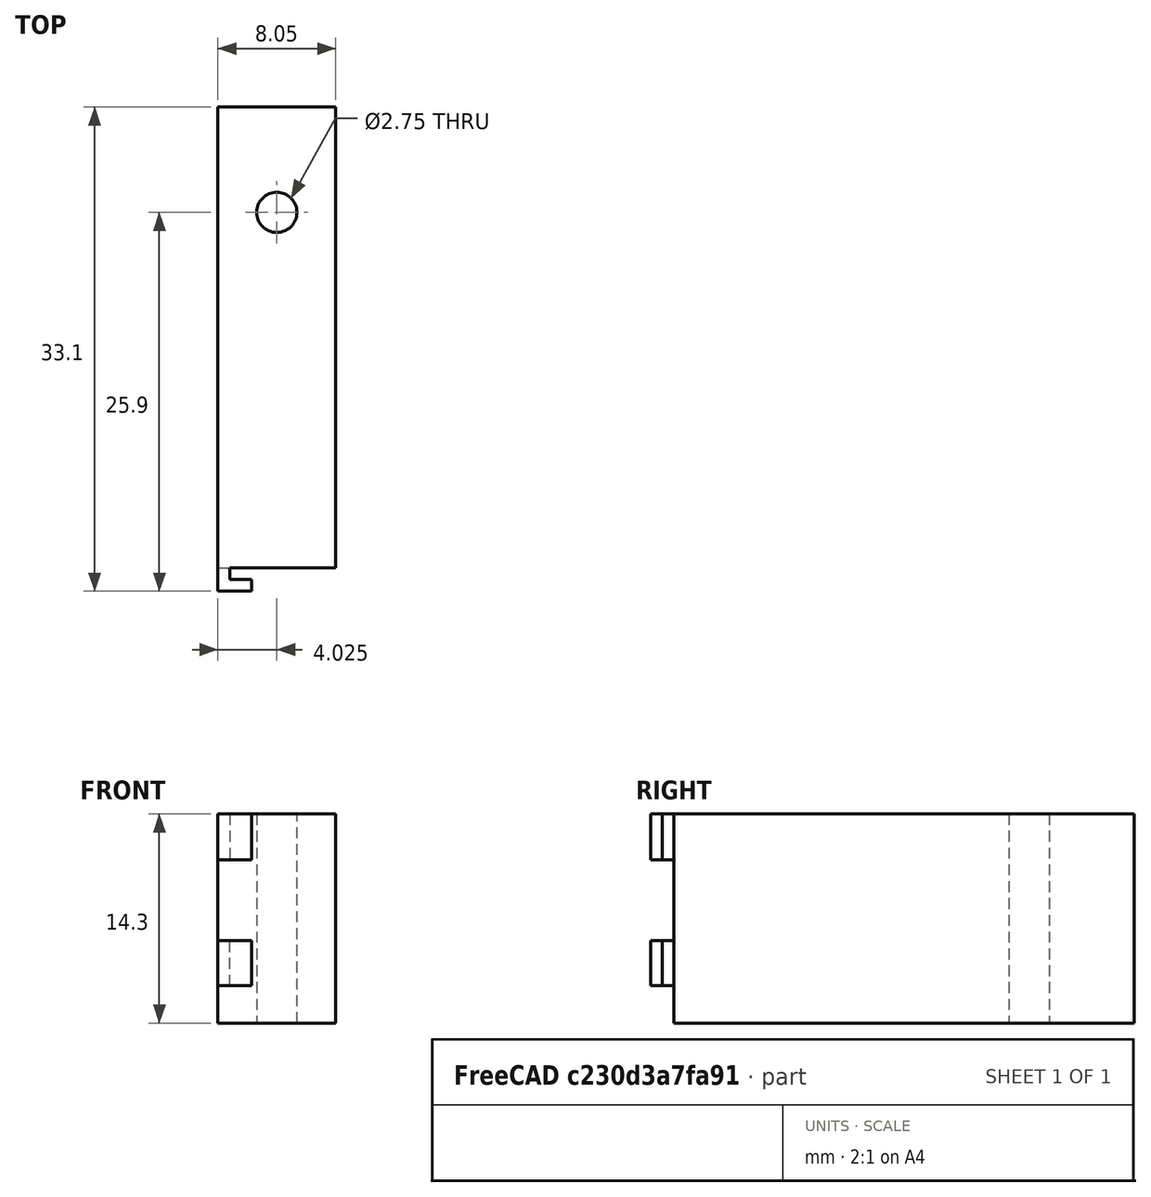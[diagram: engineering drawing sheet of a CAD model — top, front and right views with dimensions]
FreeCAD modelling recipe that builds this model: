
FCSTD DOCUMENT  (FreeCAD 0.19R)
Label: Retention Bracket
License: All rights reserved
LicenseURL: http://en.wikipedia.org/wiki/All_rights_reserved
objects: Sketcher::SketchObject×3, PartDesign::Pad×3, PartDesign::Body×1, Mesh::Feature×1
note: 10 computed .brp shape members not serialized (recipe doc carries the construction recipe); baked Part::Feature solids carry a one-line shape summary decoded from their .brp

FEATURE [Sketcher::SketchObject] Sketch
  FullyConstrained = true
  MapMode = 5
  Support = -> [XY_Plane]
  sketch-geometry (7):
    g0: LineSegment StartX=0 StartY=0 StartZ=0 EndX=8.05 EndY=0 EndZ=0
    g1: LineSegment StartX=8.05 StartY=0 StartZ=0 EndX=8.05 EndY=31.5 EndZ=0
    g2: LineSegment StartX=8.05 StartY=31.5 StartZ=0 EndX=0 EndY=31.5 EndZ=0
    g3: LineSegment StartX=0 StartY=31.5 StartZ=0 EndX=0 EndY=0 EndZ=0
    g4: Circle CenterX=4.025 CenterY=24.3 CenterZ=0 NormalX=0 NormalY=0 NormalZ=1 AngleXU=0 Radius=1.375
    g5: LineSegment StartX=4.025 StartY=24.3 StartZ=0 EndX=0 EndY=24.3 EndZ=0
    g6: LineSegment StartX=4.025 StartY=24.3 StartZ=0 EndX=8.05 EndY=24.3 EndZ=0
  constraints (20):
    c: Coincident(g0,g1)
    c: Coincident(g1,g2)
    c: Coincident(g2,g3)
    c: Coincident(g3,g0)
    c: Horizontal(g0)
    c: Horizontal(g2)
    c: Vertical(g1)
    c: Vertical(g3)
    c: Coincident(g0,g-1)
    c: DistanceY(g1,g1) = 31.5
    c: DistanceX(g2,g2) = 8.05
    c: Radius(g4) = 1.375
    c: Coincident(g5,g4)
    c: PointOnObject(g5,g3)
    c: Horizontal(g5)
    c: Coincident(g6,g4)
    c: PointOnObject(g6,g1)
    c: Horizontal(g6)
    c: Equal(g5,g6)
    c: DistanceY(g0,g4) = 24.3
FEATURE [PartDesign::Pad] Pad
  Direction = (1,1,1)
  Length = 14.3
  Length2 = 100
  Profile = -> Sketch
  Type = 0
FEATURE [Sketcher::SketchObject] Sketch001
  ExternalGeometry = -> [Pad]
  FullyConstrained = true
  MapMode = 5
  Placement = pos=(0,0,0) rot=(1,0,0;1.5708rad)
  Support = -> [Pad]
  sketch-geometry (8):
    g0: LineSegment StartX=0 StartY=14.3 StartZ=0 EndX=0.8 EndY=14.3 EndZ=0
    g1: LineSegment StartX=0.8 StartY=14.3 StartZ=0 EndX=0.8 EndY=11.15 EndZ=0
    g2: LineSegment StartX=0.8 StartY=11.15 StartZ=0 EndX=0 EndY=11.15 EndZ=0
    g3: LineSegment StartX=0 StartY=11.15 StartZ=0 EndX=0 EndY=14.3 EndZ=0
    g4: LineSegment StartX=0 StartY=2.55 StartZ=0 EndX=0.8 EndY=2.55 EndZ=0
    g5: LineSegment StartX=0.8 StartY=2.55 StartZ=0 EndX=0.8 EndY=5.65 EndZ=0
    g6: LineSegment StartX=0.8 StartY=5.65 StartZ=0 EndX=0 EndY=5.65 EndZ=0
    g7: LineSegment StartX=0 StartY=5.65 StartZ=0 EndX=0 EndY=2.55 EndZ=0
  constraints (23):
    c: Coincident(g0,g1)
    c: Coincident(g1,g2)
    c: Coincident(g2,g3)
    c: Coincident(g3,g0)
    c: Horizontal(g0)
    c: Horizontal(g2)
    c: Vertical(g1)
    c: Vertical(g3)
    c: Coincident(g4,g5)
    c: Coincident(g5,g6)
    c: Coincident(g6,g7)
    c: Coincident(g7,g4)
    c: Horizontal(g4)
    c: Horizontal(g6)
    c: Vertical(g5)
    c: Vertical(g7)
    c: PointOnObject(g4,g-3)
    c: DistanceY(g1,g1) = 3.15
    c: DistanceY(g5,g5) = 3.1
    c: DistanceY(g5,g1) = 5.5
    c: Vertical(g1,g5)
    c: DistanceX(g0,g0) = 0.8
    c: Coincident(g0,g-3)
FEATURE [PartDesign::Pad] Pad001
  BaseFeature = -> Pad
  Direction = (1,1,1)
  Length = 1.6
  Length2 = 100
  Profile = -> Sketch001
  Type = 0
FEATURE [Sketcher::SketchObject] Sketch002
  ExternalGeometry = -> [Pad001]
  FullyConstrained = true
  MapMode = 5
  Placement = pos=(0.8,0,0) rot=(0.57735,0.57735,0.57735;2.0944rad)
  Support = -> [Pad001]
  sketch-geometry (8):
    g0: LineSegment StartX=-1.6 StartY=14.3 StartZ=0 EndX=-0.8 EndY=14.3 EndZ=0
    g1: LineSegment StartX=-0.8 StartY=14.3 StartZ=0 EndX=-0.8 EndY=11.15 EndZ=0
    g2: LineSegment StartX=-0.8 StartY=11.15 StartZ=0 EndX=-1.6 EndY=11.15 EndZ=0
    g3: LineSegment StartX=-1.6 StartY=11.15 StartZ=0 EndX=-1.6 EndY=14.3 EndZ=0
    g4: LineSegment StartX=-1.6 StartY=5.65 StartZ=0 EndX=-0.8 EndY=5.65 EndZ=0
    g5: LineSegment StartX=-0.8 StartY=5.65 StartZ=0 EndX=-0.8 EndY=2.55 EndZ=0
    g6: LineSegment StartX=-0.8 StartY=2.55 StartZ=0 EndX=-1.6 EndY=2.55 EndZ=0
    g7: LineSegment StartX=-1.6 StartY=2.55 StartZ=0 EndX=-1.6 EndY=5.65 EndZ=0
  constraints (20):
    c: Coincident(g0,g1)
    c: Coincident(g1,g2)
    c: Coincident(g2,g3)
    c: Coincident(g3,g0)
    c: Horizontal(g0)
    c: Horizontal(g2)
    c: Vertical(g1)
    c: Coincident(g0,g-3)
    c: Coincident(g2,g-3)
    c: DistanceX(g0,g0) = 0.8
    c: Coincident(g4,g5)
    c: Coincident(g5,g6)
    c: Coincident(g6,g7)
    c: Coincident(g7,g4)
    c: Horizontal(g4)
    c: Horizontal(g6)
    c: Vertical(g5)
    c: Coincident(g4,g-4)
    c: Coincident(g6,g-4)
    c: DistanceX(g4,g4) = 0.8
FEATURE [PartDesign::Pad] Pad002
  BaseFeature = -> Pad001
  Direction = (1,1,1)
  Length = 1.5
  Length2 = 100
  Profile = -> Sketch002
  Type = 0
FEATURE [PartDesign::Body] Body
  Group = -> [Sketch,Pad,Sketch001,Pad001,Sketch002,Pad002]
  Origin = -> Origin
  Tip = -> Pad002
FEATURE [Mesh::Feature] Mesh  label="Pad002 (Meshed)"
